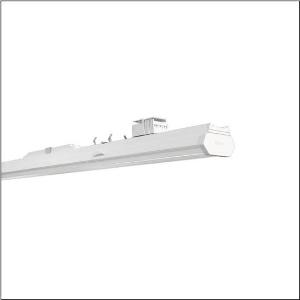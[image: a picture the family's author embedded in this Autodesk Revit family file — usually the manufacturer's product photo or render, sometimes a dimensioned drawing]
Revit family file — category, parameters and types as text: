
# Revit family: licross_21_protected_mo_52td127n485g
name_source: partatom
category: Lighting Fixtures
units: mm (PartAtom-declared; Revit-internal decimal feet)

## family parameters
Cut with Voids When Loaded = No
Host = Face
Light Source = No
Part Type = Normal
Room Calculation Point = No
Round Connector Dimension = Use Diameter
Shared = No

## types (1)
- Licross 21 Protected MO (1 x LED, 8610 lm, 47.9 W, 4000K)
    Apparent Load = 48 VA
    CIE Flux Codes = 73 92 98 99 100
    Color Rendering = 80
    Color Temperature = 4000K
    Default Elevation = 1800 mm
    Description = Licross 21 Protected MO, luminaire insert, of sheet steel, galvanised, coil coated, white, length: 1.500mm, width: 90mm, height: 101mm, LED rated luminous flux: 8.610lm, light colour: 840, SDCM (Standard Deviation of Colour Matching)MacAdam ≤ 3 SDCM (initial), control gear: ON/OFF, with plug, 3-pole, with phase selection, mains connection: 220..240V, AC, 50/60Hz, rated input power: 48W, internal wiring halogen-free, primary light control with lens, of plastic, primary optical cover: cover, of PMMA, light emission: direct distribution, primary light characteristic: symmetric, protection rating (complete): IP54, insulation class (complete): insulation class I (protective earthing), certification: CE, ENEC, VDE, UKCA, protection symbol: D if used in an environment with non-conductive dust loads with corresponding accessories, impact resistance: IK06, permissible ambient temperature for indoor applications: -35..+45°C, corresponds to IFS (International Featured Standards) requirements for safety and quality in the food industry, reducing of maximum allowable ambient temperature of 5°C with ceiling mounting, LABS conformity tested according to VDMA 24364:2018-05, The light source and the operating device comply with the requirements of the Ecodesign Regulation (EU) 2019/2020 and are replaceable in accordance with this regulation, packaging unit: 1 piece
    Height = 92 mm
    Lamp = 1 x LED
    Lamp Light Flux = 8610 lm
    Lamp Power = 47.9 W
    Lamp count = 1
    Length = 1500 mm
    Luminous efficacy = 180 lm/W
    Manufacturer = Siteco
    ModVariant = No
    Model = 52TD127N485G
    Mounting Place = Ceiling
    Mounting Type = Pendant
    Number of Poles = 1
    OnlyDefault = Yes
    Power Factor = 1
    Product Name = Licross 21 Protected MO
    Product group = luminaire insert | ceiling pendant
    ProductGroupID = 901
    Protection Class = Protection class I
    Protection Degree = IP 54
    RLX_Detail_Level = 1
    RLX_Emergency_Light_Flux = 0 lm
    RLX_Emergency_Type = 0
    RLX_Emergency_Type_DB = No
    RlxData = <blob elided: 20941 chars, md5=6dff920f>
    Socket = socket
    Standby Power = 0 W
    System Light Flux = 8610 lm
    System Power = 48 W
    Type Comments = Product without accessories
    Type Image = l_1256148.jpg
    URL = http://relux.com
    VarID = ---
    Voltage = 0 V
    Weight = 0.00 kg
    Width = 88 mm

## geometry (parser evidence)
native form markers: Blend x4, Sweep x12
no freeform markers — native parametric forms only
